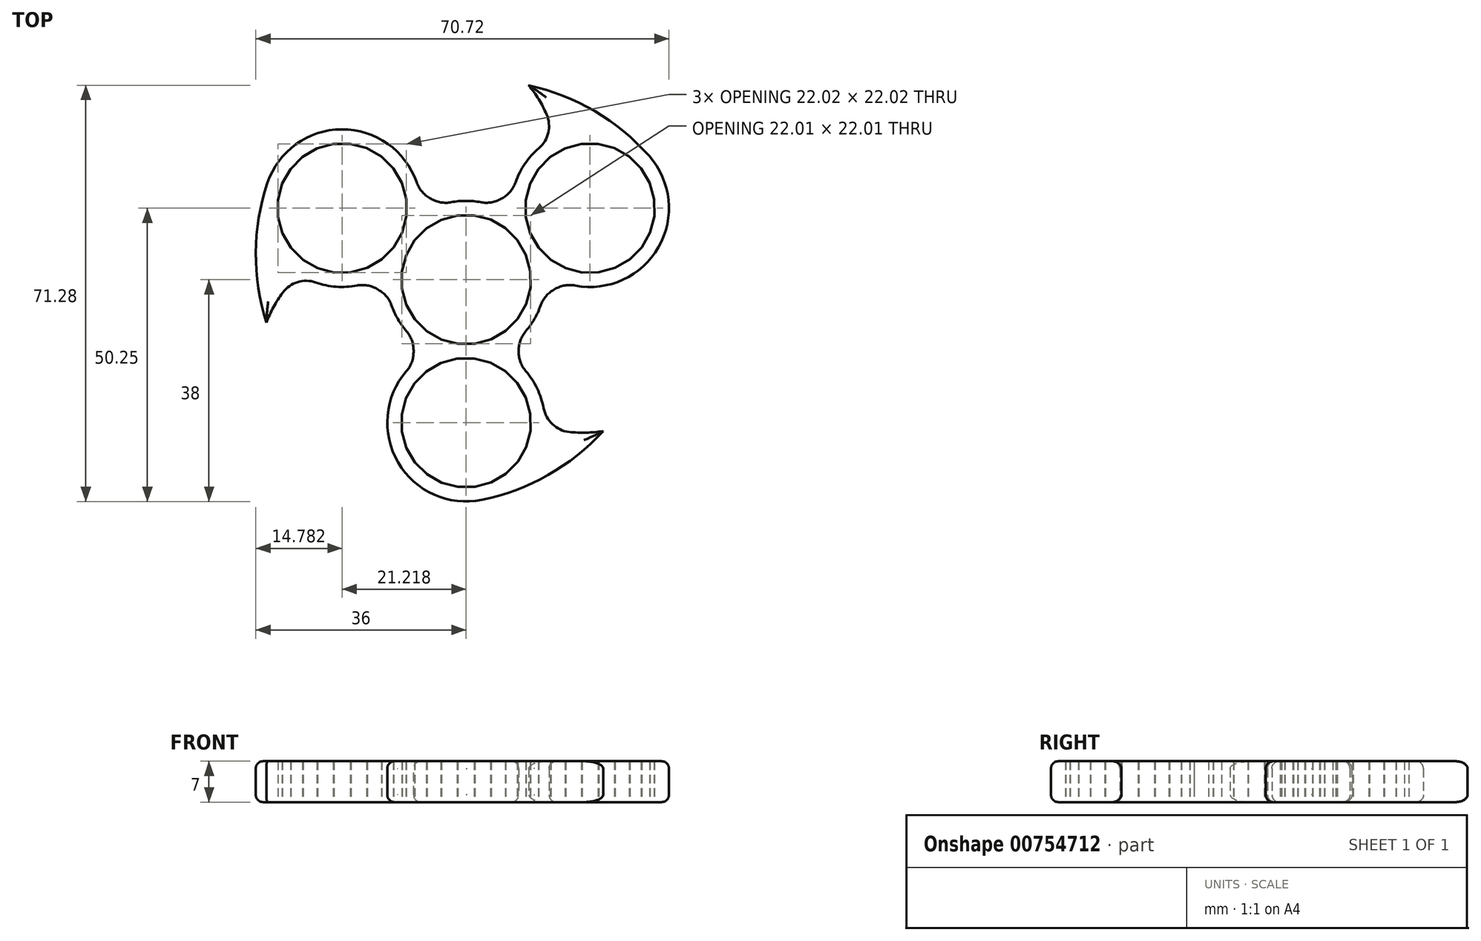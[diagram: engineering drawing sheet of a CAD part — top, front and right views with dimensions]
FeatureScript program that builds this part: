
annotation { "Feature Type Name" : "Feature", "Feature Type Description" : "" }
export const myFeature = defineFeature(function(context is Context, id is Id, definition is map)
    precondition{}
    {
        {
            var Q0;
            Q0=qCreatedBy(makeId("Front.planeOp"),FACE);
            var sketch = newSketch(context, id + "F0", { "sketchPlane" : qUnion([Q0])});
            skLineSegment(sketch, "E0", {"start": v(0, 0) * mm, "end": v(0, 6.84) * mm, "construction": true});
            skSolve(sketch);
        }
        {
            var Q0;
            Q0=qCreatedBy(makeId("Top.planeOp"),FACE);
            var sketch = newSketch(context, id + "F1", { "sketchPlane" : qUnion([Q0])});
            skCircle(sketch, "E1", {"center": v(0, 0) * mm, "radius": 13.5 * mm});
            skCircle(sketch, "E2", {"center": v(0, -24.5) * mm, "radius": 13.5 * mm});
            skLineSegment(sketch, "E3", {"start": v(0, 0) * mm, "end": v(0, -24.5) * mm, "construction": true});
            skLineSegment(sketch, "E4", {"start": v(0, 0) * mm, "end": v(20, -4.79) * mm, "construction": true});
            skArc(sketch, "E5", {"start": v(2.7, -37.73) * mm, "mid": v(14.01, -33.48) * mm, "end": v(23.46, -25.94) * mm});
            skArc(sketch, "E6", {"start": v(23.46, -25.94) * mm, "mid": v(18.43, -26.16) * mm, "end": v(13.48, -25.2) * mm});
            skCircle(sketch, "E7", {"center": v(0, 0) * mm, "radius": 38 * mm, "construction": true});
            skLineSegment(sketch, "E8", {"start": v(0, -14.94) * mm, "end": v(9, -14.94) * mm, "construction": true});
            skLineSegment(sketch, "E9", {"start": v(9, -10.06) * mm, "end": v(9, -14.44) * mm});
            skCircle(sketch, "E10.cCircle", {"center": v(0, -24.5) * mm, "radius": 11 * mm, "construction": true});
            skLineSegment(sketch, "E10.0", {"start": v(-8.84, -17.8) * mm, "end": v(-6.8, -15.74) * mm});
            skLineSegment(sketch, "E10.1", {"start": v(-6.8, -15.74) * mm, "end": v(-4.3, -14.28) * mm});
            skLineSegment(sketch, "E10.2", {"start": v(-4.3, -14.28) * mm, "end": v(-1.52, -13.5) * mm});
            skLineSegment(sketch, "E10.3", {"start": v(-1.52, -13.5) * mm, "end": v(1.38, -13.5) * mm});
            skLineSegment(sketch, "E10.4", {"start": v(1.38, -13.5) * mm, "end": v(4.18, -14.22) * mm});
            skLineSegment(sketch, "E10.5", {"start": v(4.18, -14.22) * mm, "end": v(6.7, -15.66) * mm});
            skLineSegment(sketch, "E10.6", {"start": v(6.7, -15.66) * mm, "end": v(8.76, -17.7) * mm});
            skLineSegment(sketch, "E10.7", {"start": v(8.76, -17.7) * mm, "end": v(10.22, -20.2) * mm});
            skLineSegment(sketch, "E10.8", {"start": v(10.22, -20.2) * mm, "end": v(11, -22.98) * mm});
            skLineSegment(sketch, "E10.9", {"start": v(11, -22.98) * mm, "end": v(11, -25.88) * mm});
            skLineSegment(sketch, "E10.10", {"start": v(11, -25.88) * mm, "end": v(10.28, -28.68) * mm});
            skLineSegment(sketch, "E10.11", {"start": v(10.28, -28.68) * mm, "end": v(8.84, -31.2) * mm});
            skLineSegment(sketch, "E10.12", {"start": v(8.84, -31.2) * mm, "end": v(6.8, -33.26) * mm});
            skLineSegment(sketch, "E10.13", {"start": v(6.8, -33.26) * mm, "end": v(4.3, -34.72) * mm});
            skLineSegment(sketch, "E10.14", {"start": v(4.3, -34.72) * mm, "end": v(1.52, -35.5) * mm});
            skLineSegment(sketch, "E10.15", {"start": v(1.52, -35.5) * mm, "end": v(-1.38, -35.5) * mm});
            skLineSegment(sketch, "E10.16", {"start": v(-1.38, -35.5) * mm, "end": v(-4.18, -34.78) * mm});
            skLineSegment(sketch, "E10.17", {"start": v(-4.18, -34.78) * mm, "end": v(-6.7, -33.34) * mm});
            skLineSegment(sketch, "E10.18", {"start": v(-6.7, -33.34) * mm, "end": v(-8.76, -31.3) * mm});
            skLineSegment(sketch, "E10.19", {"start": v(-8.76, -31.3) * mm, "end": v(-10.22, -28.8) * mm});
            skLineSegment(sketch, "E10.20", {"start": v(-10.22, -28.8) * mm, "end": v(-11, -26.02) * mm});
            skLineSegment(sketch, "E10.21", {"start": v(-11, -26.02) * mm, "end": v(-11, -23.12) * mm});
            skLineSegment(sketch, "E10.22", {"start": v(-11, -23.12) * mm, "end": v(-10.28, -20.32) * mm});
            skLineSegment(sketch, "E10.23", {"start": v(-10.28, -20.32) * mm, "end": v(-8.84, -17.8) * mm});
            skPoint(sketch, "E10.0.midPoint", {"position": v(-7.83, -16.77) * mm});
            skCircle(sketch, "E11.cCircle", {"center": v(0, 0) * mm, "radius": 11 * mm, "construction": true});
            skLineSegment(sketch, "E11.0", {"start": v(10.27, -4.2) * mm, "end": v(8.83, -6.72) * mm});
            skLineSegment(sketch, "E11.1", {"start": v(8.83, -6.72) * mm, "end": v(6.79, -8.78) * mm});
            skLineSegment(sketch, "E11.2", {"start": v(6.79, -8.78) * mm, "end": v(4.28, -10.23) * mm});
            skLineSegment(sketch, "E11.3", {"start": v(4.28, -10.23) * mm, "end": v(1.49, -11) * mm});
            skLineSegment(sketch, "E11.4", {"start": v(1.49, -11) * mm, "end": v(-1.4, -11) * mm});
            skLineSegment(sketch, "E11.5", {"start": v(-1.4, -11) * mm, "end": v(-4.2, -10.27) * mm});
            skLineSegment(sketch, "E11.6", {"start": v(-4.2, -10.27) * mm, "end": v(-6.72, -8.83) * mm});
            skLineSegment(sketch, "E11.7", {"start": v(-6.72, -8.83) * mm, "end": v(-8.78, -6.79) * mm});
            skLineSegment(sketch, "E11.8", {"start": v(-8.78, -6.79) * mm, "end": v(-10.23, -4.28) * mm});
            skLineSegment(sketch, "E11.9", {"start": v(-10.23, -4.28) * mm, "end": v(-11, -1.49) * mm});
            skLineSegment(sketch, "E11.10", {"start": v(-11, -1.49) * mm, "end": v(-11, 1.4) * mm});
            skLineSegment(sketch, "E11.11", {"start": v(-11, 1.4) * mm, "end": v(-10.27, 4.2) * mm});
            skLineSegment(sketch, "E11.12", {"start": v(-10.27, 4.2) * mm, "end": v(-8.83, 6.72) * mm});
            skLineSegment(sketch, "E11.13", {"start": v(-8.83, 6.72) * mm, "end": v(-6.79, 8.78) * mm});
            skLineSegment(sketch, "E11.14", {"start": v(-6.79, 8.78) * mm, "end": v(-4.28, 10.23) * mm});
            skLineSegment(sketch, "E11.15", {"start": v(-4.28, 10.23) * mm, "end": v(-1.49, 11) * mm});
            skLineSegment(sketch, "E11.16", {"start": v(-1.49, 11) * mm, "end": v(1.4, 11) * mm});
            skLineSegment(sketch, "E11.17", {"start": v(1.4, 11) * mm, "end": v(4.2, 10.27) * mm});
            skLineSegment(sketch, "E11.18", {"start": v(4.2, 10.27) * mm, "end": v(6.72, 8.83) * mm});
            skLineSegment(sketch, "E11.19", {"start": v(6.72, 8.83) * mm, "end": v(8.78, 6.79) * mm});
            skLineSegment(sketch, "E11.20", {"start": v(8.78, 6.79) * mm, "end": v(10.23, 4.28) * mm});
            skLineSegment(sketch, "E11.21", {"start": v(10.23, 4.28) * mm, "end": v(11, 1.49) * mm});
            skLineSegment(sketch, "E11.22", {"start": v(11, 1.49) * mm, "end": v(11, -1.4) * mm});
            skLineSegment(sketch, "E11.23", {"start": v(11, -1.4) * mm, "end": v(10.27, -4.2) * mm});
            skPoint(sketch, "E11.0.midPoint", {"position": v(9.55, -5.46) * mm});
            skLineSegment(sketch, "E12.MirrorCS", {"start": v(-9, -10.06) * mm, "end": v(-9, -14.44) * mm});
            skSolve(sketch);
        }
        {
            var Q0;
            {var subQ0=sQuery(id+"F7.2.F1.wireOp",EDGE,"E5");Q0=makeQuery(id+"F7.2.F1.imprint","IMPRINT",FACE,{"disambiguationData":[TD([[makeQuery(id+"F7.2.F1.imprint","IMPRINT",EDGE,{"derivedFrom":subQ0}),1.0]])]});}
            var Q1;
            Q1=makeQuery(id+"F7.2.F1.imprint","IMPRINT",FACE,{"disambiguationData":[TD([[makeQuery(id+"F7.2.F1.imprint","IMPRINT",EDGE,{"derivedFrom":sQuery(id+"F7.2.F1.wireOp",EDGE,"4f9a8486-b123-4b49-8572-80e140cb9289.0")}),1.0]])]});
            var Q2;
            {var subQ0=sQuery(id+"F7.1.F1.wireOp",EDGE,"E5");Q2=makeQuery(id+"F7.1.F1.imprint","IMPRINT",FACE,{"disambiguationData":[TD([[makeQuery(id+"F7.1.F1.imprint","IMPRINT",EDGE,{"derivedFrom":subQ0}),1.0]])]});}
            var Q3;
            Q3=makeQuery(id+"F7.1.F1.imprint","IMPRINT",FACE,{"disambiguationData":[TD([[makeQuery(id+"F7.1.F1.imprint","IMPRINT",EDGE,{"derivedFrom":sQuery(id+"F7.1.F1.wireOp",EDGE,"4f9a8486-b123-4b49-8572-80e140cb9289.0")}),1.0]])]});
            var Q4;
            {var subQ0=sQuery(id+"F1.wireOp",EDGE,"E5");Q4=makeQuery(id+"F1.imprint","IMPRINT",FACE,{"disambiguationData":[TD([[makeQuery(id+"F1.imprint","IMPRINT",EDGE,{"derivedFrom":subQ0}),1.0]])]});}
            var Q5;
            Q5=makeQuery(id+"F1.imprint","IMPRINT",FACE,{"disambiguationData":[TD([[makeQuery(id+"F1.imprint","IMPRINT",EDGE,{"derivedFrom":sQuery(id+"F1.wireOp",EDGE,"4f9a8486-b123-4b49-8572-80e140cb9289.0")}),1.0]])]});
            var Q6;
            Q6=makeQuery(id+"F1.imprint","IMPRINT",FACE,{"disambiguationData":[TD([[makeQuery(id+"F1.imprint","IMPRINT",EDGE,{"derivedFrom":sQuery(id+"F1.wireOp",EDGE,"2560e637-2683-43e8-9925-753a42ea28f2.0")}),1.0]])]});
            var Q7;
            Q7=makeQuery(id+"F7.1.F1.imprint","IMPRINT",FACE,{"disambiguationData":[TD([[makeQuery(id+"F7.1.F1.imprint","IMPRINT",EDGE,{"derivedFrom":sQuery(id+"F7.1.F1.wireOp",EDGE,"2560e637-2683-43e8-9925-753a42ea28f2.0")}),1.0]])]});
            var Q8;
            {var subQ0=sQuery(id+"F1.wireOp",EDGE,"DrzMomVu-kDaj-QfuU-c2II-xi2gSvl0tcqo");Q8=makeQuery(id+"F1.imprint","IMPRINT",FACE,{"disambiguationData":[TD([[makeQuery(id+"F1.imprint","IMPRINT",EDGE,{"derivedFrom":subQ0}),1.0]])]});}
            var Q9;
            {var subQ0=sQuery(id+"F1.wireOp",EDGE,"E9");Q9=makeQuery(id+"F1.imprint","IMPRINT",FACE,{"disambiguationData":[TD([[makeQuery(id+"F1.imprint","IMPRINT",EDGE,{"derivedFrom":subQ0}),-1.0]])]});}
            var Q10;
            {var subQ0=sQuery(id+"F7.1.F1.wireOp",EDGE,"DrzMomVu-kDaj-QfuU-c2II-xi2gSvl0tcqo");Q10=makeQuery(id+"F7.1.F1.imprint","IMPRINT",FACE,{"disambiguationData":[TD([[makeQuery(id+"F7.1.F1.imprint","IMPRINT",EDGE,{"derivedFrom":subQ0}),1.0]])]});}
            var Q11;
            {var subQ0=sQuery(id+"F7.1.F1.wireOp",EDGE,"E9");Q11=makeQuery(id+"F7.1.F1.imprint","IMPRINT",FACE,{"disambiguationData":[TD([[makeQuery(id+"F7.1.F1.imprint","IMPRINT",EDGE,{"derivedFrom":subQ0}),-1.0]])]});}
            var Q12;
            {var subQ0=sQuery(id+"F7.2.F1.wireOp",EDGE,"DrzMomVu-kDaj-QfuU-c2II-xi2gSvl0tcqo");Q12=makeQuery(id+"F7.2.F1.imprint","IMPRINT",FACE,{"disambiguationData":[TD([[makeQuery(id+"F7.2.F1.imprint","IMPRINT",EDGE,{"derivedFrom":subQ0}),1.0]])]});}
            var Q13;
            {var subQ0=sQuery(id+"F7.2.F1.wireOp",EDGE,"E9");Q13=makeQuery(id+"F7.2.F1.imprint","IMPRINT",FACE,{"disambiguationData":[TD([[makeQuery(id+"F7.2.F1.imprint","IMPRINT",EDGE,{"derivedFrom":subQ0}),-1.0]])]});}
            var Q14;
            {var subQ3=sQuery(id+"F1.wireOp",EDGE,"E2");var subQ7=sQuery(id+"F1.wireOp",EDGE,"2560e637-2683-43e8-9925-753a42ea28f2.3");var subQ10=makeQuery(id+"F1.imprint","INTERSECT",VERTEX,{"disambiguationData":[OD(0.0)],"derivedFrom":[subQ7,subQ3]});Q14=makeQuery(id+"F1.imprint","IMPRINT",FACE,{"disambiguationData":[TD([[makeQuery(id+"F1.imprint","IMPRINT",EDGE,{"disambiguationData":[TD([[subQ10,-1.0]])],"derivedFrom":subQ7}),1.0]])]});}
            var Q15;
            {var subQ0=sQuery(id+"F1.wireOp",EDGE,"E6");var subQ1=sQuery(id+"F1.wireOp",EDGE,"E2");var subQ2=makeQuery(id+"F1.imprint","INTERSECT",VERTEX,{"derivedFrom":[subQ1,subQ0]});Q15=makeQuery(id+"F1.imprint","IMPRINT",FACE,{"disambiguationData":[TD([[makeQuery(id+"F1.imprint","IMPRINT",EDGE,{"disambiguationData":[TD([[subQ2,1.0]])],"derivedFrom":subQ1}),-1.0]])]});}
            var Q16;
            {var subQ0=sQuery(id+"F7.1.F1.wireOp",EDGE,"E6");var subQ1=sQuery(id+"F7.1.F1.wireOp",EDGE,"E2");var subQ2=makeQuery(id+"F7.1.F1.imprint","INTERSECT",VERTEX,{"derivedFrom":[subQ1,subQ0]});Q16=makeQuery(id+"F7.1.F1.imprint","IMPRINT",FACE,{"disambiguationData":[TD([[makeQuery(id+"F7.1.F1.imprint","IMPRINT",EDGE,{"disambiguationData":[TD([[subQ2,1.0]])],"derivedFrom":subQ1}),-1.0]])]});}
            var Q17;
            {var subQ0=sQuery(id+"F7.2.F1.wireOp",EDGE,"E6");var subQ1=sQuery(id+"F7.2.F1.wireOp",EDGE,"E2");var subQ2=makeQuery(id+"F7.2.F1.imprint","INTERSECT",VERTEX,{"derivedFrom":[subQ1,subQ0]});Q17=makeQuery(id+"F7.2.F1.imprint","IMPRINT",FACE,{"disambiguationData":[TD([[makeQuery(id+"F7.2.F1.imprint","IMPRINT",EDGE,{"disambiguationData":[TD([[subQ2,1.0]])],"derivedFrom":subQ1}),-1.0]])]});}
            var Q18;
            {var subQ0=sQuery(id+"F1.wireOp",EDGE,"d4f3cc6e-2a77-4fe8-8df0-e3c80cf5eabb.0");var subQ1=sQuery(id+"F1.wireOp",EDGE,"E2");var subQ2=makeQuery(id+"F1.imprint","INTERSECT",VERTEX,{"derivedFrom":[subQ1,subQ0]});Q18=makeQuery(id+"F1.imprint","IMPRINT",FACE,{"disambiguationData":[TD([[makeQuery(id+"F1.imprint","IMPRINT",EDGE,{"disambiguationData":[TD([[subQ2,-1.0]])],"derivedFrom":subQ1}),-1.0]])]});}
            var Q19;
            {var subQ0=sQuery(id+"F7.2.F1.wireOp",EDGE,"d4f3cc6e-2a77-4fe8-8df0-e3c80cf5eabb.0");var subQ1=sQuery(id+"F7.2.F1.wireOp",EDGE,"E2");var subQ2=makeQuery(id+"F7.2.F1.imprint","INTERSECT",VERTEX,{"derivedFrom":[subQ1,subQ0]});Q19=makeQuery(id+"F7.2.F1.imprint","IMPRINT",FACE,{"disambiguationData":[TD([[makeQuery(id+"F7.2.F1.imprint","IMPRINT",EDGE,{"disambiguationData":[TD([[subQ2,-1.0]])],"derivedFrom":subQ1}),-1.0]])]});}
            var Q20;
            {var subQ0=sQuery(id+"F7.1.F1.wireOp",EDGE,"d4f3cc6e-2a77-4fe8-8df0-e3c80cf5eabb.0");var subQ1=sQuery(id+"F7.1.F1.wireOp",EDGE,"E2");var subQ2=makeQuery(id+"F7.1.F1.imprint","INTERSECT",VERTEX,{"derivedFrom":[subQ1,subQ0]});Q20=makeQuery(id+"F7.1.F1.imprint","IMPRINT",FACE,{"disambiguationData":[TD([[makeQuery(id+"F7.1.F1.imprint","IMPRINT",EDGE,{"disambiguationData":[TD([[subQ2,-1.0]])],"derivedFrom":subQ1}),-1.0]])]});}
            var Q21;
            {var subQ3=sQuery(id+"F1.wireOp",EDGE,"E2");var subQ8=sQuery(id+"F1.wireOp",EDGE,"2560e637-2683-43e8-9925-753a42ea28f2.4");var subQ10=makeQuery(id+"F1.imprint","INTERSECT",VERTEX,{"disambiguationData":[OD(0.0)],"derivedFrom":[subQ8,subQ3]});Q21=makeQuery(id+"F1.imprint","IMPRINT",FACE,{"disambiguationData":[TD([[makeQuery(id+"F1.imprint","IMPRINT",EDGE,{"disambiguationData":[TD([[subQ10,-1.0]])],"derivedFrom":subQ8}),1.0]])]});}
            var Q22;
            Q22=makeQuery(id+"F1.imprint","IMPRINT",FACE,{"disambiguationData":[TD([[makeQuery(id+"F1.imprint","IMPRINT",EDGE,{"derivedFrom":sQuery(id+"F1.wireOp",EDGE,"1fd2e813-266d-4ce2-8540-2a2df5a5e7ec.0")}),1.0]])]});
            var Q23;
            Q23=makeQuery(id+"F1.imprint","IMPRINT",FACE,{"disambiguationData":[TD([[makeQuery(id+"F1.imprint","IMPRINT",EDGE,{"derivedFrom":sQuery(id+"F1.wireOp",EDGE,"b8f83fdb-175d-4386-a11f-d1b9dc528f6b.0")}),1.0]])]});
            var Q24;
            {var subQ0=sQuery(id+"F1.wireOp",EDGE,"E2");var subQ1=sQuery(id+"F1.wireOp",EDGE,"E1");var subQ2=makeQuery(id+"F1.imprint","INTERSECT",VERTEX,{"disambiguationData":[OD(0.0)],"derivedFrom":[subQ1,subQ0]});Q24=makeQuery(id+"F1.imprint","IMPRINT",FACE,{"disambiguationData":[TD([[makeQuery(id+"F1.imprint","IMPRINT",EDGE,{"disambiguationData":[TD([[subQ2,-1.0]])],"derivedFrom":subQ1}),1.0]])]});}
            var Q25;
            Q25=makeQuery(id+"F1.imprint","IMPRINT",FACE,{"disambiguationData":[TD([[makeQuery(id+"F1.imprint","IMPRINT",EDGE,{"derivedFrom":sQuery(id+"F1.wireOp",EDGE,"E10.0")}),1.0]])]});
            var Q26;
            Q26=makeQuery(id+"F1.imprint","IMPRINT",FACE,{"disambiguationData":[TD([[makeQuery(id+"F1.imprint","IMPRINT",EDGE,{"derivedFrom":sQuery(id+"F1.wireOp",EDGE,"E11.0")}),1.0]])]});
            var Q27;
            Q27=sQuery(id+"F7.2.F1.wireOp",EDGE,"E2");
            extrude(context, id + "F2", {"entities" : qUnion([Q0, Q1, Q2, Q3, Q4, Q5, Q6, Q7, Q8, Q9, Q10, Q11, Q12, Q13, Q14, Q15, Q16, Q17, Q18, Q19, Q20, Q21, Q22, Q23, Q24, Q25, Q26]), "surfaceEntities" : qUnion([Q27]), "depth" : 7 * mm, "offsetDistance" : 25 * mm});
        }
        {
            var Q0;
            Q0=makeQuery(id+"F7.2.F2.opExtrude","SWEPT_EDGE",EDGE,{"disambiguationData":[OSD([sQuery(id+"F1.wireOp",EDGE,"E2"),sQuery(id+"F1.wireOp",EDGE,"E6")])]});
            var Q1;
            Q1=makeQuery(id+"F2.opExtrude","SWEPT_EDGE",EDGE,{"disambiguationData":[OSD([sQuery(id+"F1.wireOp",EDGE,"E2"),sQuery(id+"F1.wireOp",EDGE,"E6")])]});
            var Q2;
            Q2=makeQuery(id+"F7.1.F2.opExtrude","SWEPT_EDGE",EDGE,{"disambiguationData":[OSD([sQuery(id+"F1.wireOp",EDGE,"E2"),sQuery(id+"F1.wireOp",EDGE,"E6")])]});
            var Q3;
            Q3=makeQuery(id+"F2.opExtrude","SWEPT_EDGE",EDGE,{"disambiguationData":[OSD([sQuery(id+"F7.1.F1.wireOp",EDGE,"E2"),sQuery(id+"F7.1.F1.wireOp",EDGE,"E6")])]});
            var Q4;
            Q4=makeQuery(id+"F2.opExtrude","SWEPT_EDGE",EDGE,{"disambiguationData":[OSD([sQuery(id+"F7.2.F1.wireOp",EDGE,"E2"),sQuery(id+"F7.2.F1.wireOp",EDGE,"E6")])]});
            fillet(context, id + "F3", {"entities" : qUnion([Q0, Q1, Q2, Q3, Q4]), "radius" : 5 * mm, "tangentPropagation" : true, "allowEdgeOverflow" : false});
        }
        {
            var Q0;
            Q0=makeQuery(id+"F2.opExtrude","SWEPT_EDGE",EDGE,{"disambiguationData":[OSD([sQuery(id+"F1.wireOp",EDGE,"E2"),sQuery(id+"F1.wireOp",EDGE,"DrzMomVu-kDaj-QfuU-c2II-xi2gSvl0tcqo")])]});
            var Q1;
            Q1=makeQuery(id+"F7.2.F2.opExtrude","SWEPT_EDGE",EDGE,{"disambiguationData":[OSD([sQuery(id+"F1.wireOp",EDGE,"E2"),sQuery(id+"F1.wireOp",EDGE,"E9")])]});
            var Q2;
            Q2=makeQuery(id+"F2.opExtrude","SWEPT_EDGE",EDGE,{"disambiguationData":[OSD([sQuery(id+"F1.wireOp",EDGE,"E2"),sQuery(id+"F1.wireOp",EDGE,"E9")])]});
            var Q3;
            Q3=makeQuery(id+"F7.1.F2.opExtrude","SWEPT_EDGE",EDGE,{"disambiguationData":[OSD([sQuery(id+"F1.wireOp",EDGE,"E2"),sQuery(id+"F1.wireOp",EDGE,"DrzMomVu-kDaj-QfuU-c2II-xi2gSvl0tcqo")])]});
            var Q4;
            Q4=makeQuery(id+"F7.2.F2.opExtrude","SWEPT_EDGE",EDGE,{"disambiguationData":[OSD([sQuery(id+"F1.wireOp",EDGE,"E2"),sQuery(id+"F1.wireOp",EDGE,"DrzMomVu-kDaj-QfuU-c2II-xi2gSvl0tcqo")])]});
            var Q5;
            Q5=makeQuery(id+"F7.1.F2.opExtrude","SWEPT_EDGE",EDGE,{"disambiguationData":[OSD([sQuery(id+"F1.wireOp",EDGE,"E2"),sQuery(id+"F1.wireOp",EDGE,"E9")])]});
            var Q6;
            Q6=makeQuery(id+"F2.opExtrude","SWEPT_EDGE",EDGE,{"disambiguationData":[OSD([sQuery(id+"F7.1.F1.wireOp",EDGE,"E2"),sQuery(id+"F7.1.F1.wireOp",EDGE,"DrzMomVu-kDaj-QfuU-c2II-xi2gSvl0tcqo")])]});
            var Q7;
            Q7=makeQuery(id+"F2.opExtrude","SWEPT_EDGE",EDGE,{"disambiguationData":[OSD([sQuery(id+"F7.2.F1.wireOp",EDGE,"E2"),sQuery(id+"F7.2.F1.wireOp",EDGE,"E9")])]});
            var Q8;
            Q8=makeQuery(id+"F2.opExtrude","SWEPT_EDGE",EDGE,{"disambiguationData":[OSD([sQuery(id+"F7.2.F1.wireOp",EDGE,"E2"),sQuery(id+"F7.2.F1.wireOp",EDGE,"DrzMomVu-kDaj-QfuU-c2II-xi2gSvl0tcqo")])]});
            var Q9;
            Q9=makeQuery(id+"F2.opExtrude","SWEPT_EDGE",EDGE,{"disambiguationData":[OSD([sQuery(id+"F7.1.F1.wireOp",EDGE,"E2"),sQuery(id+"F7.1.F1.wireOp",EDGE,"E9")])]});
            fillet(context, id + "F4", {"entities" : qUnion([Q0, Q1, Q2, Q3, Q4, Q5, Q6, Q7, Q8, Q9]), "radius" : 5 * mm, "tangentPropagation" : true, "allowEdgeOverflow" : false});
        }
        {
            var Q0;
            Q0=makeQuery(id+"F2.opExtrude","SWEPT_EDGE",EDGE,{"disambiguationData":[OSD([sQuery(id+"F1.wireOp",EDGE,"E1"),sQuery(id+"F1.wireOp",EDGE,"DrzMomVu-kDaj-QfuU-c2II-xi2gSvl0tcqo")])]});
            var Q1;
            Q1=makeQuery(id+"F2.opExtrude","SWEPT_EDGE",EDGE,{"disambiguationData":[OSD([sQuery(id+"F1.wireOp",EDGE,"E1"),sQuery(id+"F1.wireOp",EDGE,"E9")])]});
            var Q2;
            Q2=makeQuery(id+"F7.1.F2.opExtrude","SWEPT_EDGE",EDGE,{"disambiguationData":[OSD([sQuery(id+"F1.wireOp",EDGE,"E1"),sQuery(id+"F1.wireOp",EDGE,"E9")])]});
            var Q3;
            Q3=makeQuery(id+"F7.2.F2.opExtrude","SWEPT_EDGE",EDGE,{"disambiguationData":[OSD([sQuery(id+"F1.wireOp",EDGE,"E1"),sQuery(id+"F1.wireOp",EDGE,"E9")])]});
            var Q4;
            Q4=makeQuery(id+"F7.2.F2.opExtrude","SWEPT_EDGE",EDGE,{"disambiguationData":[OSD([sQuery(id+"F1.wireOp",EDGE,"E1"),sQuery(id+"F1.wireOp",EDGE,"DrzMomVu-kDaj-QfuU-c2II-xi2gSvl0tcqo")])]});
            var Q5;
            Q5=makeQuery(id+"F7.1.F2.opExtrude","SWEPT_EDGE",EDGE,{"disambiguationData":[OSD([sQuery(id+"F1.wireOp",EDGE,"E1"),sQuery(id+"F1.wireOp",EDGE,"DrzMomVu-kDaj-QfuU-c2II-xi2gSvl0tcqo")])]});
            var Q6;
            {var subQ0=sQuery(id+"F1.wireOp",EDGE,"E1");var subQ1=makeQuery(id+"F2.opExtrude","SWEPT_FACE",FACE,{"disambiguationData":[OSD([subQ0]),TDD([makeQuery(id+"F1.imprint","IMPRINT",EDGE,{"disambiguationData":[TD([[makeQuery(id+"F1.imprint","INTERSECT",VERTEX,{"derivedFrom":[subQ0,sQuery(id+"F1.wireOp",EDGE,"DrzMomVu-kDaj-QfuU-c2II-xi2gSvl0tcqo")]}),1.0]])],"derivedFrom":subQ0})])]});var subQ2=sQuery(id+"F7.1.F1.wireOp",EDGE,"E1");Q6=makeQuery(id+"FjCtKf3FRhO1t0G_3.opBoolean","INTERSECT",EDGE,{"disambiguationData":[topologyDisambiguationEdgeConnected([makeQuery(id+"F2.opExtrude","SWEPT_FACE",FACE,{"disambiguationData":[OSD([sQuery(id+"F7.2.F1.wireOp",EDGE,"E9")])]})])],"derivedFrom":[subQ1,makeQuery(id+"F2.opExtrude","SWEPT_FACE",FACE,{"disambiguationData":[OSD([subQ2]),TDD([makeQuery(id+"F7.1.F1.imprint","IMPRINT",EDGE,{"disambiguationData":[TD([[makeQuery(id+"F7.1.F1.imprint","INTERSECT",VERTEX,{"derivedFrom":[subQ2,sQuery(id+"F7.1.F1.wireOp",EDGE,"DrzMomVu-kDaj-QfuU-c2II-xi2gSvl0tcqo")]}),1.0]])],"derivedFrom":subQ2})])]})]});}
            var Q7;
            {var subQ0=sQuery(id+"F1.wireOp",EDGE,"E1");var subQ1=makeQuery(id+"F2.opExtrude","SWEPT_FACE",FACE,{"disambiguationData":[OSD([subQ0]),TDD([makeQuery(id+"F1.imprint","IMPRINT",EDGE,{"disambiguationData":[TD([[makeQuery(id+"F1.imprint","INTERSECT",VERTEX,{"derivedFrom":[subQ0,sQuery(id+"F1.wireOp",EDGE,"DrzMomVu-kDaj-QfuU-c2II-xi2gSvl0tcqo")]}),1.0]])],"derivedFrom":subQ0})])]});var subQ2=sQuery(id+"F7.1.F1.wireOp",EDGE,"E1");Q7=makeQuery(id+"FjCtKf3FRhO1t0G_3.opBoolean","INTERSECT",EDGE,{"disambiguationData":[topologyDisambiguationEdgeConnected([makeQuery(id+"F2.opExtrude","SWEPT_FACE",FACE,{"disambiguationData":[OSD([sQuery(id+"F7.2.F1.wireOp",EDGE,"DrzMomVu-kDaj-QfuU-c2II-xi2gSvl0tcqo")])]})])],"derivedFrom":[subQ1,makeQuery(id+"F2.opExtrude","SWEPT_FACE",FACE,{"disambiguationData":[OSD([subQ2]),TDD([makeQuery(id+"F7.1.F1.imprint","IMPRINT",EDGE,{"disambiguationData":[TD([[makeQuery(id+"F7.1.F1.imprint","INTERSECT",VERTEX,{"derivedFrom":[subQ2,sQuery(id+"F7.1.F1.wireOp",EDGE,"DrzMomVu-kDaj-QfuU-c2II-xi2gSvl0tcqo")]}),1.0]])],"derivedFrom":subQ2})])]})]});}
            var Q8;
            Q8=makeQuery(id+"F2.opExtrude","SWEPT_EDGE",EDGE,{"disambiguationData":[OSD([sQuery(id+"F7.1.F1.wireOp",EDGE,"E1"),sQuery(id+"F7.1.F1.wireOp",EDGE,"E9")])]});
            var Q9;
            Q9=makeQuery(id+"F2.opExtrude","SWEPT_EDGE",EDGE,{"disambiguationData":[OSD([sQuery(id+"F7.1.F1.wireOp",EDGE,"E1"),sQuery(id+"F7.1.F1.wireOp",EDGE,"DrzMomVu-kDaj-QfuU-c2II-xi2gSvl0tcqo")])]});
            fillet(context, id + "F5", {"entities" : qUnion([Q0, Q1, Q2, Q3, Q4, Q5, Q6, Q7, Q8, Q9]), "radius" : 5 * mm, "tangentPropagation" : true, "allowEdgeOverflow" : false});
        }
        {
            var Q0;
            Q0=makeQuery(id+"F2.opExtrude","CAP_EDGE",EDGE,{"disambiguationData":[OSD([sQuery(id+"F1.wireOp",EDGE,"E5")])],"isStart":false});
            var Q1;
            Q1=makeQuery(id+"F2.opExtrude","CAP_EDGE",EDGE,{"disambiguationData":[OSD([sQuery(id+"F1.wireOp",EDGE,"E5")])],"isStart":true});
            var Q2;
            Q2=makeQuery(id+"F2.opExtrude","CAP_EDGE",EDGE,{"disambiguationData":[OSD([sQuery(id+"F7.1.F1.wireOp",EDGE,"E5")])],"isStart":false});
            var Q3;
            Q3=makeQuery(id+"F2.opExtrude","CAP_EDGE",EDGE,{"disambiguationData":[OSD([sQuery(id+"F7.1.F1.wireOp",EDGE,"E5")])],"isStart":true});
            var Q4;
            Q4=makeQuery(id+"F2.opExtrude","CAP_EDGE",EDGE,{"disambiguationData":[OSD([sQuery(id+"F7.2.F1.wireOp",EDGE,"E5")])],"isStart":false});
            var Q5;
            Q5=makeQuery(id+"F2.opExtrude","CAP_EDGE",EDGE,{"disambiguationData":[OSD([sQuery(id+"F7.2.F1.wireOp",EDGE,"E5")])],"isStart":true});
            fillet(context, id + "F6", {"entities" : qUnion([Q0, Q1, Q2, Q3, Q4, Q5]), "radius" : 1.25 * mm, "tangentPropagation" : true, "allowEdgeOverflow" : false});
        }
        {
            var Q0;
            Q0=makeQuery(id+"F2.opExtrude","SWEPT_BODY",BODY,{"disambiguationData":[OSD([sQuery(id+"F1.wireOp",EDGE,"2560e637-2683-43e8-9925-753a42ea28f2.0"),sQuery(id+"F1.wireOp",EDGE,"2560e637-2683-43e8-9925-753a42ea28f2.1"),sQuery(id+"F1.wireOp",EDGE,"2560e637-2683-43e8-9925-753a42ea28f2.2"),sQuery(id+"F1.wireOp",EDGE,"2560e637-2683-43e8-9925-753a42ea28f2.3"),sQuery(id+"F1.wireOp",EDGE,"2560e637-2683-43e8-9925-753a42ea28f2.4"),sQuery(id+"F1.wireOp",EDGE,"2560e637-2683-43e8-9925-753a42ea28f2.5"),sQuery(id+"F1.wireOp",EDGE,"2560e637-2683-43e8-9925-753a42ea28f2.6"),sQuery(id+"F1.wireOp",EDGE,"2560e637-2683-43e8-9925-753a42ea28f2.7"),sQuery(id+"F1.wireOp",EDGE,"2560e637-2683-43e8-9925-753a42ea28f2.8"),sQuery(id+"F1.wireOp",EDGE,"2560e637-2683-43e8-9925-753a42ea28f2.9"),sQuery(id+"F1.wireOp",EDGE,"2560e637-2683-43e8-9925-753a42ea28f2.10"),sQuery(id+"F1.wireOp",EDGE,"2560e637-2683-43e8-9925-753a42ea28f2.11"),sQuery(id+"F1.wireOp",EDGE,"2560e637-2683-43e8-9925-753a42ea28f2.12"),sQuery(id+"F1.wireOp",EDGE,"2560e637-2683-43e8-9925-753a42ea28f2.13"),sQuery(id+"F1.wireOp",EDGE,"2560e637-2683-43e8-9925-753a42ea28f2.14"),sQuery(id+"F1.wireOp",EDGE,"2560e637-2683-43e8-9925-753a42ea28f2.15"),sQuery(id+"F1.wireOp",EDGE,"2560e637-2683-43e8-9925-753a42ea28f2.16"),sQuery(id+"F1.wireOp",EDGE,"2560e637-2683-43e8-9925-753a42ea28f2.17"),sQuery(id+"F1.wireOp",EDGE,"2560e637-2683-43e8-9925-753a42ea28f2.18"),sQuery(id+"F1.wireOp",EDGE,"2560e637-2683-43e8-9925-753a42ea28f2.19"),sQuery(id+"F1.wireOp",EDGE,"2560e637-2683-43e8-9925-753a42ea28f2.20"),sQuery(id+"F1.wireOp",EDGE,"2560e637-2683-43e8-9925-753a42ea28f2.21"),sQuery(id+"F1.wireOp",EDGE,"2560e637-2683-43e8-9925-753a42ea28f2.22"),sQuery(id+"F1.wireOp",EDGE,"2560e637-2683-43e8-9925-753a42ea28f2.23"),sQuery(id+"F1.wireOp",EDGE,"2560e637-2683-43e8-9925-753a42ea28f2.24"),sQuery(id+"F1.wireOp",EDGE,"2560e637-2683-43e8-9925-753a42ea28f2.25"),sQuery(id+"F1.wireOp",EDGE,"2560e637-2683-43e8-9925-753a42ea28f2.26"),sQuery(id+"F1.wireOp",EDGE,"2560e637-2683-43e8-9925-753a42ea28f2.27"),sQuery(id+"F1.wireOp",EDGE,"2560e637-2683-43e8-9925-753a42ea28f2.28"),sQuery(id+"F1.wireOp",EDGE,"2560e637-2683-43e8-9925-753a42ea28f2.29"),sQuery(id+"F1.wireOp",EDGE,"2560e637-2683-43e8-9925-753a42ea28f2.30"),sQuery(id+"F1.wireOp",EDGE,"2560e637-2683-43e8-9925-753a42ea28f2.31"),sQuery(id+"F1.wireOp",EDGE,"2560e637-2683-43e8-9925-753a42ea28f2.32"),sQuery(id+"F1.wireOp",EDGE,"2560e637-2683-43e8-9925-753a42ea28f2.33"),sQuery(id+"F1.wireOp",EDGE,"2560e637-2683-43e8-9925-753a42ea28f2.34"),sQuery(id+"F1.wireOp",EDGE,"2560e637-2683-43e8-9925-753a42ea28f2.35"),sQuery(id+"F1.wireOp",EDGE,"4f9a8486-b123-4b49-8572-80e140cb9289.0"),sQuery(id+"F1.wireOp",EDGE,"4f9a8486-b123-4b49-8572-80e140cb9289.1"),sQuery(id+"F1.wireOp",EDGE,"4f9a8486-b123-4b49-8572-80e140cb9289.2"),sQuery(id+"F1.wireOp",EDGE,"4f9a8486-b123-4b49-8572-80e140cb9289.3"),sQuery(id+"F1.wireOp",EDGE,"4f9a8486-b123-4b49-8572-80e140cb9289.4"),sQuery(id+"F1.wireOp",EDGE,"4f9a8486-b123-4b49-8572-80e140cb9289.5"),sQuery(id+"F1.wireOp",EDGE,"4f9a8486-b123-4b49-8572-80e140cb9289.6"),sQuery(id+"F1.wireOp",EDGE,"4f9a8486-b123-4b49-8572-80e140cb9289.7"),sQuery(id+"F1.wireOp",EDGE,"4f9a8486-b123-4b49-8572-80e140cb9289.8"),sQuery(id+"F1.wireOp",EDGE,"4f9a8486-b123-4b49-8572-80e140cb9289.9"),sQuery(id+"F1.wireOp",EDGE,"4f9a8486-b123-4b49-8572-80e140cb9289.10"),sQuery(id+"F1.wireOp",EDGE,"4f9a8486-b123-4b49-8572-80e140cb9289.11"),sQuery(id+"F1.wireOp",EDGE,"4f9a8486-b123-4b49-8572-80e140cb9289.12"),sQuery(id+"F1.wireOp",EDGE,"4f9a8486-b123-4b49-8572-80e140cb9289.13"),sQuery(id+"F1.wireOp",EDGE,"4f9a8486-b123-4b49-8572-80e140cb9289.14"),sQuery(id+"F1.wireOp",EDGE,"4f9a8486-b123-4b49-8572-80e140cb9289.15"),sQuery(id+"F1.wireOp",EDGE,"4f9a8486-b123-4b49-8572-80e140cb9289.16"),sQuery(id+"F1.wireOp",EDGE,"4f9a8486-b123-4b49-8572-80e140cb9289.17"),sQuery(id+"F1.wireOp",EDGE,"4f9a8486-b123-4b49-8572-80e140cb9289.18"),sQuery(id+"F1.wireOp",EDGE,"4f9a8486-b123-4b49-8572-80e140cb9289.19"),sQuery(id+"F1.wireOp",EDGE,"4f9a8486-b123-4b49-8572-80e140cb9289.20"),sQuery(id+"F1.wireOp",EDGE,"4f9a8486-b123-4b49-8572-80e140cb9289.21"),sQuery(id+"F1.wireOp",EDGE,"4f9a8486-b123-4b49-8572-80e140cb9289.22"),sQuery(id+"F1.wireOp",EDGE,"4f9a8486-b123-4b49-8572-80e140cb9289.23"),sQuery(id+"F1.wireOp",EDGE,"4f9a8486-b123-4b49-8572-80e140cb9289.24"),sQuery(id+"F1.wireOp",EDGE,"4f9a8486-b123-4b49-8572-80e140cb9289.25"),sQuery(id+"F1.wireOp",EDGE,"4f9a8486-b123-4b49-8572-80e140cb9289.26"),sQuery(id+"F1.wireOp",EDGE,"4f9a8486-b123-4b49-8572-80e140cb9289.27"),sQuery(id+"F1.wireOp",EDGE,"4f9a8486-b123-4b49-8572-80e140cb9289.28"),sQuery(id+"F1.wireOp",EDGE,"4f9a8486-b123-4b49-8572-80e140cb9289.29"),sQuery(id+"F1.wireOp",EDGE,"4f9a8486-b123-4b49-8572-80e140cb9289.30"),sQuery(id+"F1.wireOp",EDGE,"4f9a8486-b123-4b49-8572-80e140cb9289.31"),sQuery(id+"F1.wireOp",EDGE,"4f9a8486-b123-4b49-8572-80e140cb9289.32"),sQuery(id+"F1.wireOp",EDGE,"4f9a8486-b123-4b49-8572-80e140cb9289.33"),sQuery(id+"F1.wireOp",EDGE,"4f9a8486-b123-4b49-8572-80e140cb9289.34"),sQuery(id+"F1.wireOp",EDGE,"4f9a8486-b123-4b49-8572-80e140cb9289.35"),sQuery(id+"F1.wireOp",EDGE,"E1"),sQuery(id+"F1.wireOp",EDGE,"E2"),sQuery(id+"F1.wireOp",EDGE,"E5"),sQuery(id+"F1.wireOp",EDGE,"E6"),sQuery(id+"F1.wireOp",EDGE,"DrzMomVu-kDaj-QfuU-c2II-xi2gSvl0tcqo"),sQuery(id+"F1.wireOp",EDGE,"E9")])]});
            var Q1;
            Q1=sQuery(id+"F0.wireOp",EDGE,"E0");
            circularPattern(context, id + "F7", {"operationType" : NewBodyOperationType.ADD, "entities" : qUnion([Q0]), "axis" : qUnion([Q1]), "angle" : 360 * degree, "instanceCount" : 3, "equalSpace" : true});
        }
    });
